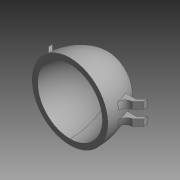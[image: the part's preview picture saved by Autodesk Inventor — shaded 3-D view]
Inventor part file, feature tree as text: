
AUTODESK INVENTOR PART (.ipt)
format: ipt  version: 2014 SP2 (Build 180246200, 246)  size: 361,472 bytes
history: native  units: mm
features: sketch x5, revolve x3, projected_geometry x3, plane x2, extrude x2, fillet x2, mirror x2, other x1
ambient origin geometry x8: Origin, YZ Plane, XZ Plane, XY Plane, X Axis, Y Axis, Z Axis, Center Point
bodies: Solid1 (feature_tree)
feature tree (20):
  revolve  "Revolution1"  Angle=90.0deg
  plane  "Work Plane1"
  extrude  "Extrusion3"  Depth=6.0mm
  extrude  "Extrusion4"  Depth=3.0mm
  fillet  "Fillet1"  Radius=8.4mm
  mirror  "Mirror5"
  mirror  "Mirror6"
  revolve  "Revolution2"  [1 undecoded]
  plane  "Work Plane3"
  other  "Work Axis1"
  revolve  "Revolution3"  [1 undecoded]
  fillet  "Fillet2"  [1 undecoded]
  sketch  "Sketch1"  dims[d2=90.0deg d5=90.0deg]
  sketch  "Sketch2"  dims[d23=0.0mm d24=6.0mm]
  sketch  "Sketch5"  dims[d25=45.0deg d26=3.0mm d27=8.4mm]
  projected_geometry  "Projected Loop2"
  sketch  "Sketch6"  dims[d28=0.0mm d29=5.0mm]
  sketch  "Sketch12"  dims[d45=7.4mm d46=28.0mm d47=90.0deg d48=5.0mm]
  projected_geometry  "Project Cut Edges2"
  projected_geometry  "Project Cut Edges6"
note: 3 required parameter values undecoded (feature->parameter linkage not recoverable at this tier; creation-order binding heuristic only, values carry confidence <= 0.55)